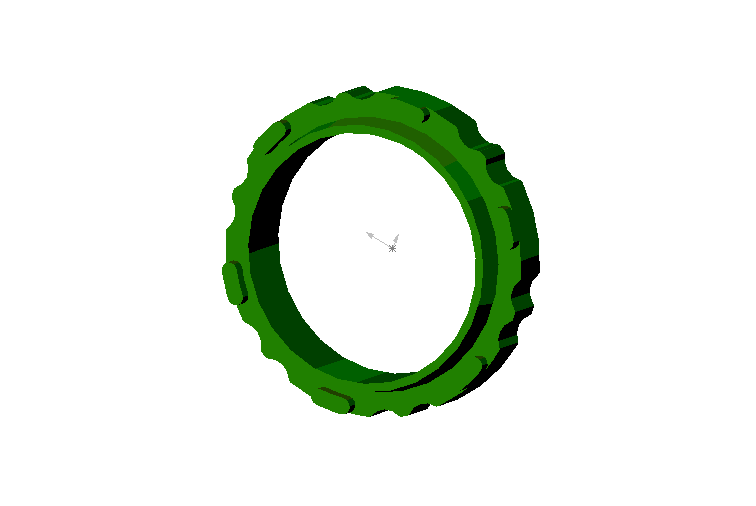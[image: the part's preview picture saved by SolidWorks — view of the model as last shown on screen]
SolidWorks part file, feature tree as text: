
SOLIDWORKS PART (.sldprt)
format: sldprt  version: not decoded by parser v0  size: 316,928 bytes
history: native  units: mm
features: sketch x4, plane x3, extrude x3, chamfer x1, revolve x1 + 1 further entry (+6 scaffold rows collapsed)
feature tree (19):
  scaffold x6  (default folders/planes/origin — collapsed)
  "Corps de surface"
  plane  "Plan1"
  plane  "Plan2"
  plane  "Plan3"
  sketch  "Esquisse1"  dims[c1.D1=30.0mm c1.D2=39.0mm c1.D5=5.0mm c1.D6=5.0mm c1.D9=0.5mm c1.D10=0.5mm c2.D9=0.5mm c2.D5=2.5mm c2.D1=30.0mm c2.D2=19.5mm c2.D3=21.0mm c2.D4=21.0mm c2.D7=21.0mm c3.D7=15.0deg c3.D8=21.0mm c4.D8=15.0deg]
  extrude  "Base-Extrusion"  Depth=5mm
  sketch  "Esquisse2"  dims[D1=33.0mm D2=30.0mm]
  extrude  "Boss.-Extru.1"  Depth=3mm
  chamfer  "Chanfrein1"  Distance=3mm
  sketch  "Esquisse3"  dims[c1.D1=39.0mm c1.D2=35.0mm c1.D7=2.0mm c1.D8=40.0mm c1.D3=20.0mm c2.D3=40.0deg c2.D4=~27.621053mm c3.D4=5.0deg c3.D5=18.5mm c3.D6=~27.621053mm c3.D8=18.5mm]
  extrude  "Boss.-Extru.2"  Depth=1.5mm
  sketch  "Esquisse5"  dims[D2=1.0mm D1=17.5mm]
  revolve  "Boss.-Révol.1"  Angle=360deg
decode coverage: 9 of 9 modeling features carry decoded parameters; 1 rows unclassified (native names shown)
note: ~ marks probable driven/reference dimensions
note: suppression state not decoded; provenance and decode notes live in map.json
